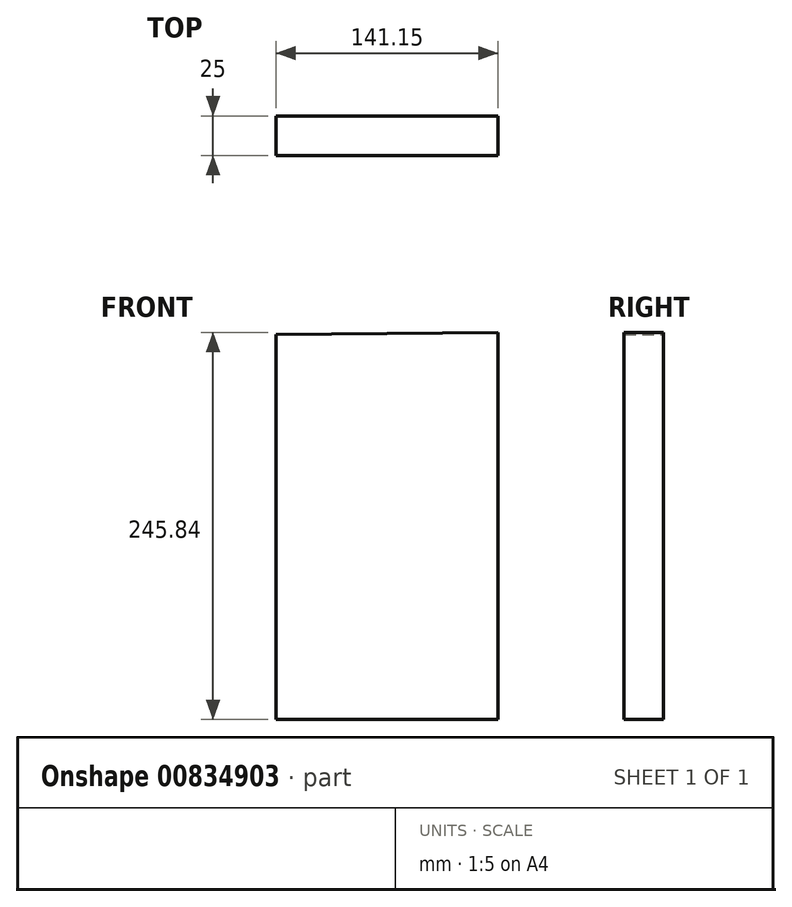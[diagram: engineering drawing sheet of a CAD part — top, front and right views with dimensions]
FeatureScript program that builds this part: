
annotation { "Feature Type Name" : "Feature", "Feature Type Description" : "" }
export const myFeature = defineFeature(function(context is Context, id is Id, definition is map)
    precondition{}
    {
        {
            var Q0;
            Q0=qCreatedBy(makeId("Front.planeOp"),FACE);
            var sketch = newSketch(context, id + "F0", { "sketchPlane" : qUnion([Q0])});
            skLineSegment(sketch, "E0", {"start": v(-75.74, 73.94) * mm, "end": v(-75.74, -170.72) * mm});
            skLineSegment(sketch, "E1", {"start": v(-75.74, -170.72) * mm, "end": v(65.41, -170.72) * mm});
            skLineSegment(sketch, "E2", {"start": v(65.41, -170.72) * mm, "end": v(65.41, 75.12) * mm});
            skLineSegment(sketch, "E3", {"start": v(65.41, 75.12) * mm, "end": v(-75.74, 73.94) * mm});
            skSolve(sketch);
        }
        {
            var Q0;
            Q0 = qSketchRegion(id + "F0", true);
            extrude(context, id + "F1", {"entities" : qUnion([Q0]), "depth" : 25 * mm, "offsetDistance" : 25 * mm});
        }
    });
